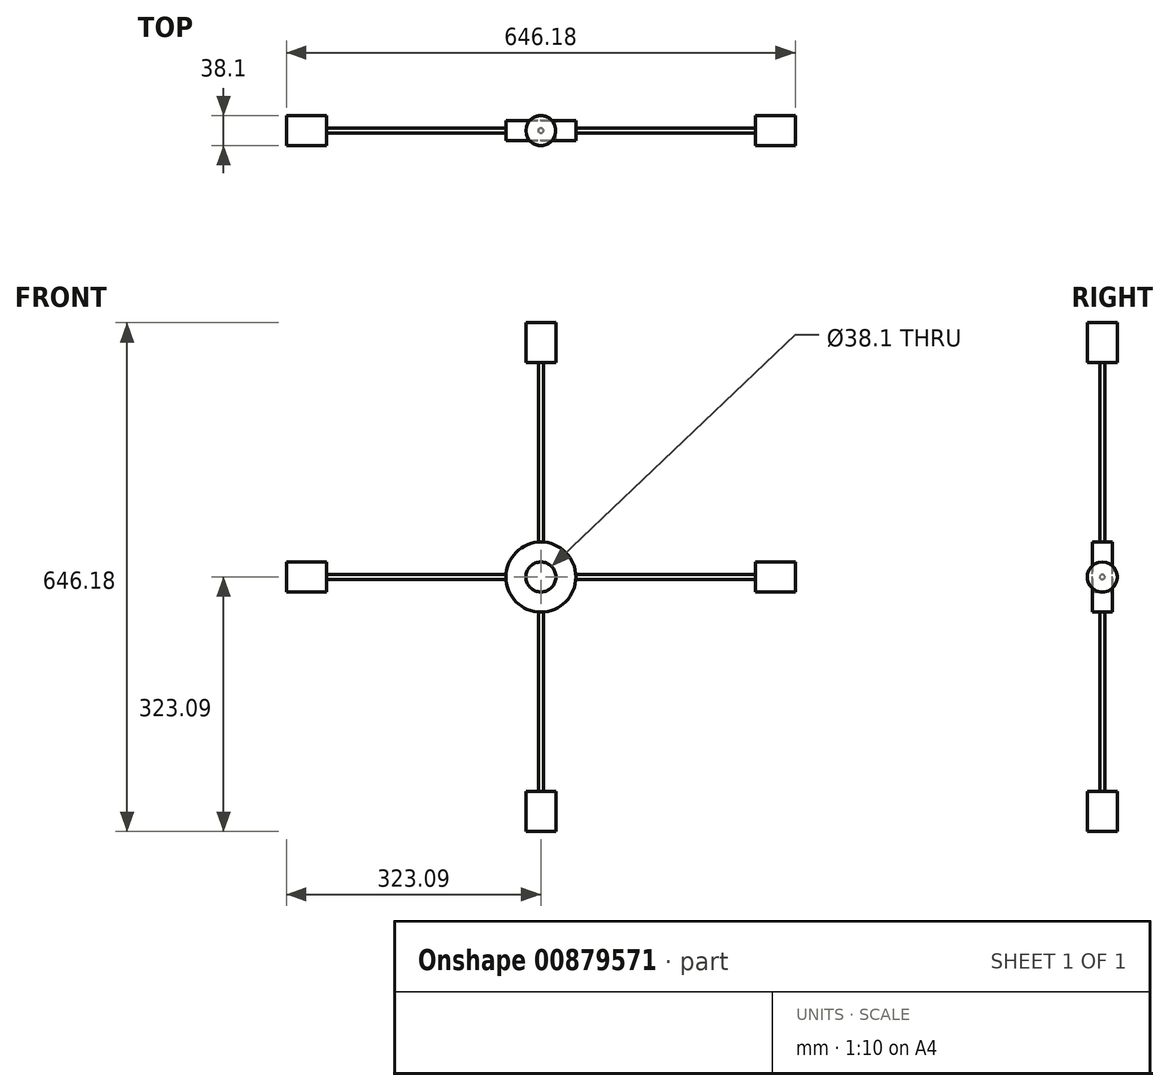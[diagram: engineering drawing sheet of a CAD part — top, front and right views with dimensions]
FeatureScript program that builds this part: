
annotation { "Feature Type Name" : "Feature", "Feature Type Description" : "" }
export const myFeature = defineFeature(function(context is Context, id is Id, definition is map)
    precondition{}
    {
        {
            var Q0;
            Q0=qCreatedBy(makeId("Front.planeOp"),FACE);
            var sketch = newSketch(context, id + "F0", { "sketchPlane" : qUnion([Q0])});
            skCircle(sketch, "E0", {"center": v(0, 0) * mm, "radius": 19.05 * mm});
            skCircle(sketch, "E1", {"center": v(0, 0) * mm, "radius": 44.45 * mm});
            skSolve(sketch);
        }
        {
            var Q0;
            Q0=qCreatedBy(makeId("Front.planeOp"),FACE);
            var sketch = newSketch(context, id + "F1", { "sketchPlane" : qUnion([Q0])});
            skLineSegment(sketch, "E2.bottom", {"start": v(-3.17, 43.69) * mm, "end": v(0, 43.69) * mm});
            skLineSegment(sketch, "E2.left", {"start": v(-3.17, 43.69) * mm, "end": v(-3.18, 287.98) * mm});
            skLineSegment(sketch, "E2.right", {"start": v(0, 43.69) * mm, "end": v(0, 272.29) * mm});
            skLineSegment(sketch, "E3.bottom", {"start": v(0, 272.29) * mm, "end": v(-19.05, 272.29) * mm});
            skLineSegment(sketch, "E3.top", {"start": v(0, 323.09) * mm, "end": v(-19.05, 323.09) * mm});
            skLineSegment(sketch, "E3.left", {"start": v(0, 272.29) * mm, "end": v(0, 323.09) * mm});
            skLineSegment(sketch, "E3.right", {"start": v(-19.05, 272.29) * mm, "end": v(-19.05, 323.09) * mm});
            skLineSegment(sketch, "E4.1.0", {"start": v(-43.69, 0) * mm, "end": v(-272.29, 0) * mm});
            skLineSegment(sketch, "E4.1.1", {"start": v(-43.69, -3.17) * mm, "end": v(-287.98, -3.18) * mm});
            skLineSegment(sketch, "E4.1.2", {"start": v(-43.69, -3.17) * mm, "end": v(-43.69, 0) * mm});
            skLineSegment(sketch, "E4.1.3", {"start": v(-272.29, 0) * mm, "end": v(-272.29, -19.05) * mm});
            skLineSegment(sketch, "E4.1.4", {"start": v(-272.29, 0) * mm, "end": v(-323.09, 0) * mm});
            skLineSegment(sketch, "E4.1.5", {"start": v(-323.09, 0) * mm, "end": v(-323.09, -19.05) * mm});
            skLineSegment(sketch, "E4.1.6", {"start": v(-272.29, -19.05) * mm, "end": v(-323.09, -19.05) * mm});
            skLineSegment(sketch, "E4.2.0", {"start": v(0, -43.69) * mm, "end": v(0, -272.29) * mm});
            skLineSegment(sketch, "E4.2.1", {"start": v(3.17, -43.69) * mm, "end": v(3.18, -287.98) * mm});
            skLineSegment(sketch, "E4.2.2", {"start": v(3.17, -43.69) * mm, "end": v(0, -43.69) * mm});
            skLineSegment(sketch, "E4.2.3", {"start": v(0, -272.29) * mm, "end": v(19.05, -272.29) * mm});
            skLineSegment(sketch, "E4.2.4", {"start": v(0, -272.29) * mm, "end": v(0, -323.09) * mm});
            skLineSegment(sketch, "E4.2.5", {"start": v(0, -323.09) * mm, "end": v(19.05, -323.09) * mm});
            skLineSegment(sketch, "E4.2.6", {"start": v(19.05, -272.29) * mm, "end": v(19.05, -323.09) * mm});
            skPoint(sketch, "E4.center", {"position": v(0, 0) * mm});
            skLineSegment(sketch, "E5.1.3.0", {"start": v(43.69, 0) * mm, "end": v(272.29, 0) * mm});
            skLineSegment(sketch, "E5.3.3.0", {"start": v(43.69, 3.17) * mm, "end": v(287.98, 3.18) * mm});
            skLineSegment(sketch, "E5.6.3.0", {"start": v(43.69, 3.17) * mm, "end": v(43.69, 0) * mm});
            skLineSegment(sketch, "E5.9.3.0", {"start": v(272.29, 0) * mm, "end": v(272.29, 19.05) * mm});
            skLineSegment(sketch, "E5.12.3.0", {"start": v(272.29, 0) * mm, "end": v(323.09, 0) * mm});
            skLineSegment(sketch, "E5.15.3.0", {"start": v(323.09, 0) * mm, "end": v(323.09, 19.05) * mm});
            skLineSegment(sketch, "E5.18.3.0", {"start": v(272.29, 19.05) * mm, "end": v(323.09, 19.05) * mm});
            skSolve(sketch);
        }
        {
            var Q0;
            Q0=makeQuery(id+"F0.imprint","IMPRINT",FACE,{"disambiguationData":[TD([[makeQuery(id+"F0.imprint","IMPRINT",EDGE,{"derivedFrom":sQuery(id+"F0.wireOp",EDGE,"E0")}),-1.0]])]});
            extrude(context, id + "F2", {"entities" : qUnion([Q0]), "endBound" : BoundingType.SYMMETRIC, "depth" : 25.4 * mm, "offsetDistance" : 25.4 * mm});
        }
        {
            var Q0;
            Q0=makeQuery(id+"F1.imprint","IMPRINT",FACE,{"disambiguationData":[TD([[makeQuery(id+"F1.imprint","IMPRINT",EDGE,{"derivedFrom":sQuery(id+"F1.wireOp",EDGE,"E2.bottom")}),1.0]])]});
            var Q1;
            Q1=makeQuery(id+"F1.imprint","IMPRINT",FACE,{"disambiguationData":[TD([[makeQuery(id+"F1.imprint","IMPRINT",EDGE,{"derivedFrom":sQuery(id+"F1.wireOp",EDGE,"E3.top")}),1.0]])]});
            var Q2;
            Q2=sQuery(id+"F1.wireOp",EDGE,"E2.right");
            revolve(context, id + "F3", {"operationType" : NewBodyOperationType.ADD, "surfaceOperationType" : NewSurfaceOperationType.NEW, "entities" : qUnion([Q0, Q1]), "axis" : qUnion([Q2]), "revolveType" : RevolveType.FULL});
        }
        {
            var Q0;
            {var subQ0=sQuery(id+"F1.wireOp",EDGE,"E5.1.3.0");Q0=makeQuery(id+"F1.imprint","IMPRINT",FACE,{"disambiguationData":[TD([[makeQuery(id+"F1.imprint","IMPRINT",EDGE,{"derivedFrom":subQ0}),1.0]])]});}
            var Q1;
            {var subQ0=sQuery(id+"F1.wireOp",EDGE,"E5.12.3.0");Q1=makeQuery(id+"F1.imprint","IMPRINT",FACE,{"disambiguationData":[TD([[makeQuery(id+"F1.imprint","IMPRINT",EDGE,{"derivedFrom":subQ0}),1.0]])]});}
            var Q2;
            Q2=sQuery(id+"F1.wireOp",EDGE,"E5.1.3.0");
            revolve(context, id + "F4", {"operationType" : NewBodyOperationType.ADD, "surfaceOperationType" : NewSurfaceOperationType.NEW, "entities" : qUnion([Q0, Q1]), "axis" : qUnion([Q2]), "revolveType" : RevolveType.FULL});
        }
        {
            var Q0;
            {var subQ0=sQuery(id+"F1.wireOp",EDGE,"E4.2.0");Q0=makeQuery(id+"F1.imprint","IMPRINT",FACE,{"disambiguationData":[TD([[makeQuery(id+"F1.imprint","IMPRINT",EDGE,{"derivedFrom":subQ0}),1.0]])]});}
            var Q1;
            {var subQ0=sQuery(id+"F1.wireOp",EDGE,"E4.2.4");Q1=makeQuery(id+"F1.imprint","IMPRINT",FACE,{"disambiguationData":[TD([[makeQuery(id+"F1.imprint","IMPRINT",EDGE,{"derivedFrom":subQ0}),1.0]])]});}
            var Q2;
            Q2=sQuery(id+"F1.wireOp",EDGE,"E4.2.4");
            revolve(context, id + "F5", {"operationType" : NewBodyOperationType.ADD, "surfaceOperationType" : NewSurfaceOperationType.NEW, "entities" : qUnion([Q0, Q1]), "axis" : qUnion([Q2]), "revolveType" : RevolveType.FULL});
        }
        {
            var Q0;
            {var subQ0=sQuery(id+"F1.wireOp",EDGE,"E4.1.4");Q0=makeQuery(id+"F1.imprint","IMPRINT",FACE,{"disambiguationData":[TD([[makeQuery(id+"F1.imprint","IMPRINT",EDGE,{"derivedFrom":subQ0}),1.0]])]});}
            var Q1;
            {var subQ0=sQuery(id+"F1.wireOp",EDGE,"E4.1.0");Q1=makeQuery(id+"F1.imprint","IMPRINT",FACE,{"disambiguationData":[TD([[makeQuery(id+"F1.imprint","IMPRINT",EDGE,{"derivedFrom":subQ0}),1.0]])]});}
            var Q2;
            Q2=sQuery(id+"F1.wireOp",EDGE,"E4.1.4");
            revolve(context, id + "F6", {"operationType" : NewBodyOperationType.ADD, "surfaceOperationType" : NewSurfaceOperationType.NEW, "entities" : qUnion([Q0, Q1]), "axis" : qUnion([Q2]), "revolveType" : RevolveType.FULL});
        }
    });
